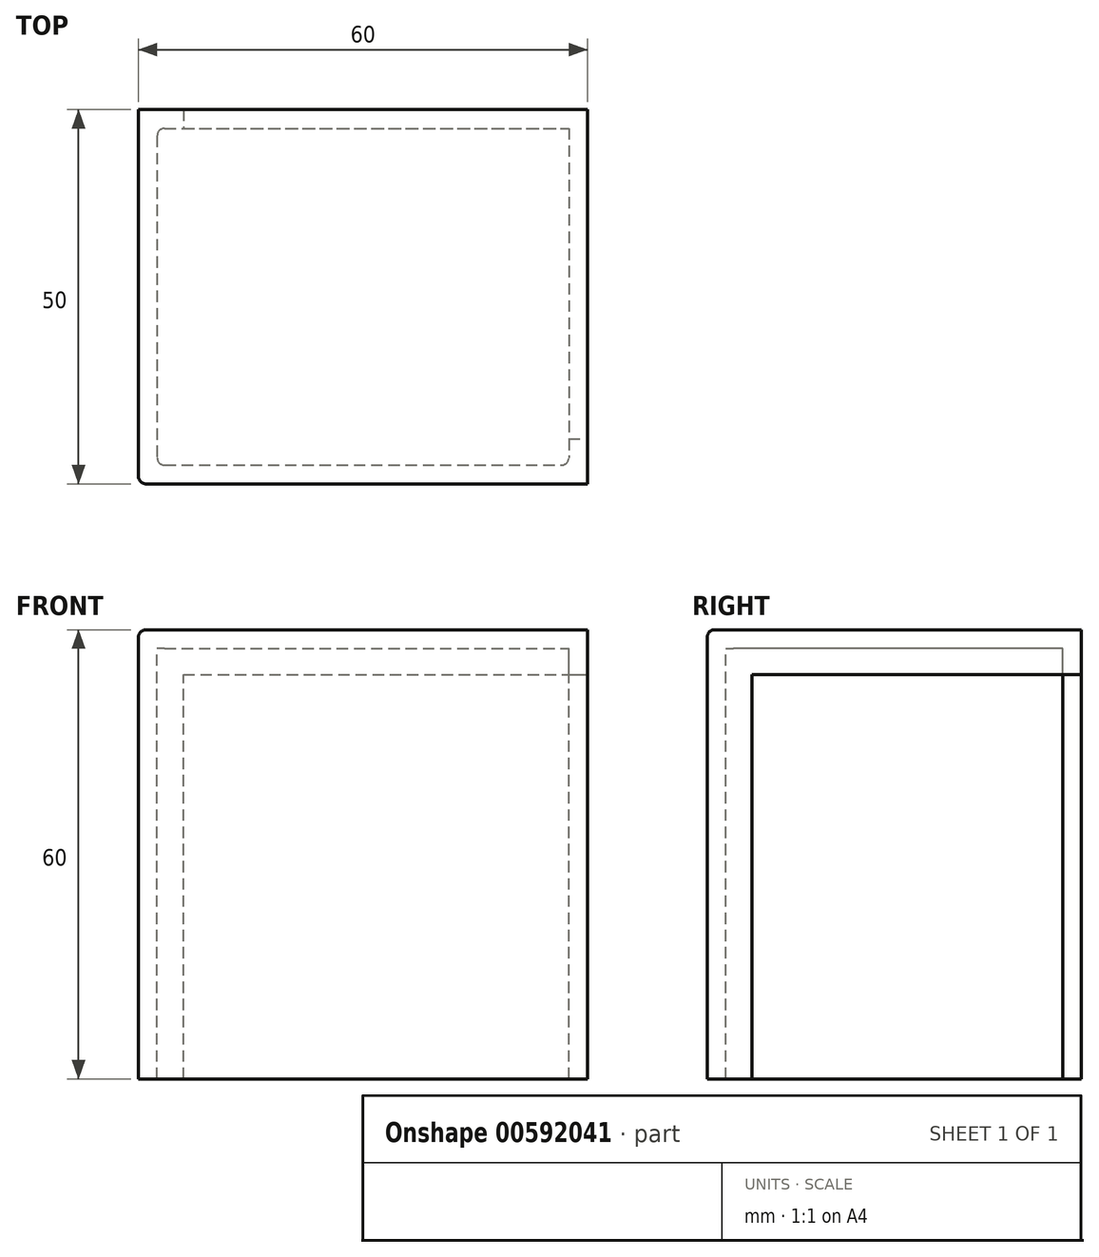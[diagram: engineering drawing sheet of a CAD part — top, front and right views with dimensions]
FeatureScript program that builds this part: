
annotation { "Feature Type Name" : "Feature", "Feature Type Description" : "" }
export const myFeature = defineFeature(function(context is Context, id is Id, definition is map)
    precondition{}
    {
        {
            var Q0;
            Q0=qCreatedBy(makeId("Top.planeOp"),FACE);
            var sketch = newSketch(context, id + "F0", { "sketchPlane" : qUnion([Q0])});
            skLineSegment(sketch, "E0.bottom", {"start": v(-30.59, 27.15) * mm, "end": v(29.41, 27.15) * mm});
            skLineSegment(sketch, "E0.top", {"start": v(-30.59, -22.85) * mm, "end": v(29.41, -22.85) * mm});
            skLineSegment(sketch, "E0.left", {"start": v(-30.59, 27.15) * mm, "end": v(-30.59, -22.85) * mm});
            skLineSegment(sketch, "E0.right", {"start": v(29.41, 27.15) * mm, "end": v(29.41, -22.85) * mm});
            skLineSegment(sketch, "E1.0", {"start": v(-28.09, 24.65) * mm, "end": v(26.91, 24.65) * mm});
            skLineSegment(sketch, "E1.1", {"start": v(-28.09, 24.65) * mm, "end": v(-28.09, -20.35) * mm});
            skLineSegment(sketch, "E1.2", {"start": v(-28.09, -20.35) * mm, "end": v(26.91, -20.35) * mm});
            skLineSegment(sketch, "E1.3", {"start": v(26.91, 24.65) * mm, "end": v(26.91, -20.35) * mm});
            skLineSegment(sketch, "E2", {"start": v(-24.59, 27.15) * mm, "end": v(-24.59, 24.65) * mm});
            skLineSegment(sketch, "E3", {"start": v(26.91, -16.85) * mm, "end": v(29.41, -16.85) * mm});
            skSolve(sketch);
        }
        {
            var Q0;
            {var subQ1=sQuery(id+"F0.wireOp",EDGE,"E1.1");Q0=makeQuery(id+"F0.imprint","IMPRINT",FACE,{"disambiguationData":[TD([[makeQuery(id+"F0.imprint","IMPRINT",EDGE,{"derivedFrom":subQ1}),1.0]])]});}
            var Q1;
            {var subQ1=sQuery(id+"F0.wireOp",EDGE,"E0.top");Q1=makeQuery(id+"F0.imprint","IMPRINT",FACE,{"disambiguationData":[TD([[makeQuery(id+"F0.imprint","IMPRINT",EDGE,{"derivedFrom":subQ1}),1.0]])]});}
            var Q2;
            {var subQ0=sQuery(id+"F0.wireOp",EDGE,"E2");Q2=makeQuery(id+"F0.imprint","IMPRINT",FACE,{"disambiguationData":[TD([[makeQuery(id+"F0.imprint","IMPRINT",EDGE,{"derivedFrom":subQ0}),1.0]])]});}
            extrude(context, id + "F1", {"entities" : qUnion([Q0, Q1, Q2]), "depth" : 2.5 * mm, "offsetDistance" : 25 * mm});
        }
        {
            var Q0;
            {var subQ1=sQuery(id+"F0.wireOp",EDGE,"E0.top");Q0=makeQuery(id+"F0.imprint","IMPRINT",FACE,{"disambiguationData":[TD([[makeQuery(id+"F0.imprint","IMPRINT",EDGE,{"derivedFrom":subQ1}),1.0]])]});}
            extrude(context, id + "F2", {"entities" : qUnion([Q0]), "operationType" : NewBodyOperationType.ADD, "oppositeDirection" : true, "depth" : 57.5 * mm, "offsetDistance" : 25 * mm});
        }
        {
            var Q0;
            {var subQ0=sQuery(id+"F0.wireOp",EDGE,"E2");Q0=makeQuery(id+"F0.imprint","IMPRINT",FACE,{"disambiguationData":[TD([[makeQuery(id+"F0.imprint","IMPRINT",EDGE,{"derivedFrom":subQ0}),1.0]])]});}
            extrude(context, id + "F3", {"entities" : qUnion([Q0]), "operationType" : NewBodyOperationType.ADD, "oppositeDirection" : true, "depth" : 3.5 * mm, "offsetDistance" : 25 * mm});
        }
        {
            var Q0;
            Q0=makeQuery(id+"F1.opExtrude","CAP_EDGE",EDGE,{"disambiguationData":[OSD([sQuery(id+"F0.wireOp",EDGE,"E0.left")])],"isStart":false});
            var Q1;
            Q1=makeQuery(id+"F1.opExtrude","CAP_EDGE",EDGE,{"disambiguationData":[OSD([sQuery(id+"F0.wireOp",EDGE,"E0.top")])],"isStart":false});
            var Q2;
            {var subQ0=sQuery(id+"F0.wireOp",EDGE,"E0.left");var subQ1=sQuery(id+"F0.wireOp",EDGE,"E0.top");Q2=makeQuery(id+"F2.boolean.opBoolean","MERGE",EDGE,{"derivedFrom":[makeQuery(id+"F1.opExtrude","SWEPT_EDGE",EDGE,{"disambiguationData":[OSD([subQ1,subQ0])]}),makeQuery(id+"F2.opExtrude","SWEPT_EDGE",EDGE,{"disambiguationData":[OSD([subQ1,subQ0])]})]});}
            var Q3;
            Q3=makeQuery(id+"F2.opExtrude","SWEPT_EDGE",EDGE,{"disambiguationData":[OSD([sQuery(id+"F0.wireOp",EDGE,"E1.1"),sQuery(id+"F0.wireOp",EDGE,"E1.2")])]});
            var Q4;
            Q4=makeQuery(id+"F2.opExtrude","SWEPT_EDGE",EDGE,{"disambiguationData":[OSD([sQuery(id+"F0.wireOp",EDGE,"E1.2"),sQuery(id+"F0.wireOp",EDGE,"E1.3")])]});
            var Q5;
            Q5=makeQuery(id+"F2.opExtrude","SWEPT_EDGE",EDGE,{"disambiguationData":[OSD([sQuery(id+"F0.wireOp",EDGE,"E1.0"),sQuery(id+"F0.wireOp",EDGE,"E1.1")])]});
            fillet(context, id + "F4", {"entities" : qUnion([Q0, Q1, Q2, Q3, Q4, Q5]), "tangentPropagation" : true, "radius" : 1 * mm, "defaultsChanged" : false, "vertexSettings" : [], "allowEdgeOverflow" : false});
        }
    });
